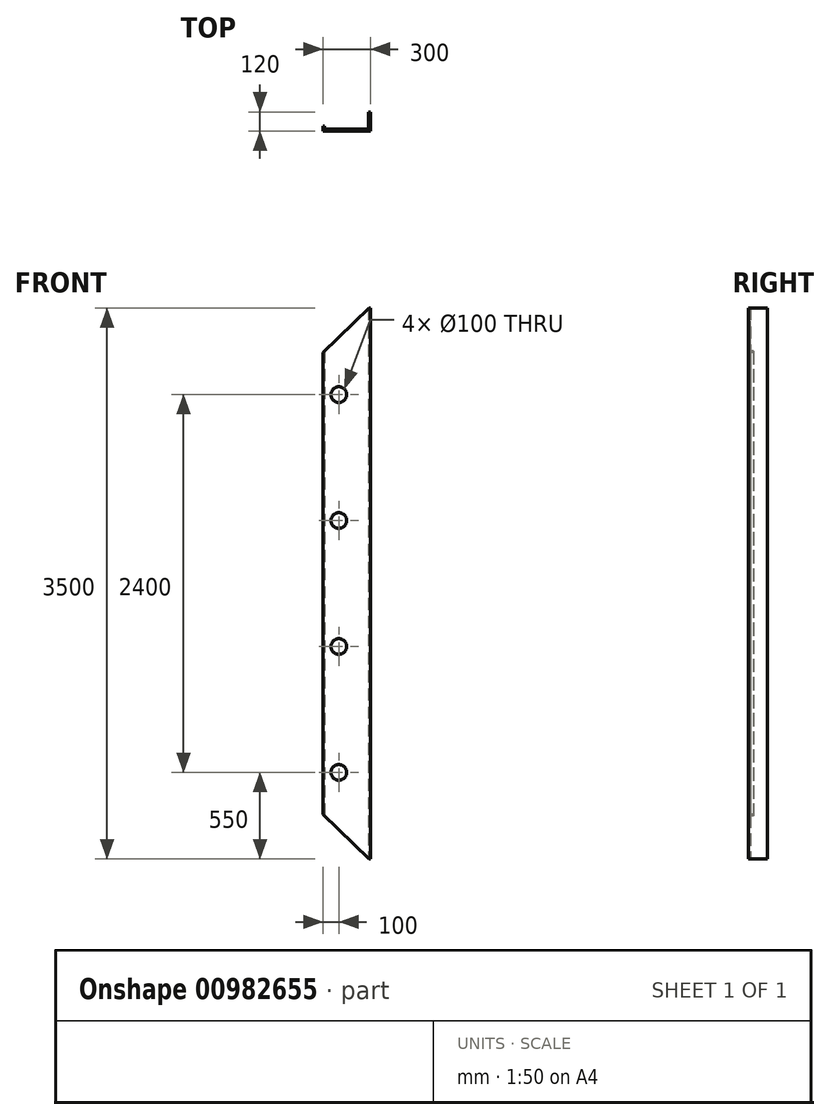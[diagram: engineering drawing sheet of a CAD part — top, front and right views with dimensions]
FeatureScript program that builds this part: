
annotation { "Feature Type Name" : "Feature", "Feature Type Description" : "" }
export const myFeature = defineFeature(function(context is Context, id is Id, definition is map)
    precondition{}
    {
        {
            var Q0;
            Q0=qCreatedBy(makeId("Top.planeOp"),FACE);
            var sketch = newSketch(context, id + "F0", { "sketchPlane" : qUnion([Q0])});
            skLineSegment(sketch, "E0", {"start": v(-110, 0) * mm, "end": v(-100, 0) * mm});
            skLineSegment(sketch, "E1", {"start": v(-100, 0) * mm, "end": v(-100, -20) * mm});
            skLineSegment(sketch, "E2", {"start": v(-100, -20) * mm, "end": v(180, -20) * mm});
            skLineSegment(sketch, "E3", {"start": v(180, -20) * mm, "end": v(180, 90) * mm});
            skLineSegment(sketch, "E4", {"start": v(180, 90) * mm, "end": v(190, 90) * mm});
            skLineSegment(sketch, "E5", {"start": v(190, 90) * mm, "end": v(190, -30) * mm});
            skLineSegment(sketch, "E6", {"start": v(190, -30) * mm, "end": v(-110, -30) * mm});
            skLineSegment(sketch, "E7", {"start": v(-110, -30) * mm, "end": v(-110, 0) * mm});
            skSolve(sketch);
        }
        {
            var Q0;
            Q0=qSketchRegion(id+"F0",true);
            extrude(context, id + "F1", {"entities" : qUnion([Q0]), "depth" : 3500 * mm, "offsetDistance" : 25 * mm});
        }
        {
            var Q0;
            Q0=makeQuery(id+"F1.opExtrude","SWEPT_FACE",FACE,{"disambiguationData":[OSD([sQuery(id+"F0.wireOp",EDGE,"E6")])]});
            var sketch = newSketch(context, id + "F2", { "sketchPlane" : qUnion([Q0])});
            skLineSegment(sketch, "E8", {"start": v(-310, 3024.02) * mm, "end": v(-310, 3700) * mm});
            skLineSegment(sketch, "E9", {"start": v(-310, 3700) * mm, "end": v(390, 3700) * mm});
            skLineSegment(sketch, "E10", {"start": v(390, 3700) * mm, "end": v(-310, 3024.02) * mm});
            skLineSegment(sketch, "E11", {"start": v(-2423.37, 1750) * mm, "end": v(3096.96, 1750) * mm});
            skLineSegment(sketch, "E12.MirrorCS", {"start": v(-310, -200) * mm, "end": v(390, -200) * mm});
            skLineSegment(sketch, "E13.MirrorCS", {"start": v(-310, 475.98) * mm, "end": v(-310, -200) * mm});
            skLineSegment(sketch, "E14.MirrorCS", {"start": v(390, -200) * mm, "end": v(-310, 475.98) * mm});
            skSolve(sketch);
        }
        {
            var Q0;
            {var subQ0=sQuery(id+"F2.wireOp",EDGE,"E14.MirrorCS");var subQ1=sQuery(id+"F0.wireOp",EDGE,"E6");var subQ2=makeQuery(id+"F1.opExtrude","CAP_EDGE",EDGE,{"disambiguationData":[OSD([subQ1])],"isStart":true});var subQ3=makeQuery(id+"F2.imprint","INTERSECT",VERTEX,{"derivedFrom":[subQ2,subQ0]});Q0=makeQuery(id+"F2.imprint","IMPRINT",FACE,{"disambiguationData":[TD([[makeQuery(id+"F2.imprint","IMPRINT",EDGE,{"disambiguationData":[TD([[subQ3,-1.0]])],"derivedFrom":subQ0}),1.0]])]});}
            var Q1;
            {var subQ0=sQuery(id+"F2.wireOp",EDGE,"E10");var subQ1=sQuery(id+"F0.wireOp",EDGE,"E6");var subQ2=makeQuery(id+"F1.opExtrude","CAP_EDGE",EDGE,{"disambiguationData":[OSD([subQ1])],"isStart":false});var subQ3=makeQuery(id+"F2.imprint","INTERSECT",VERTEX,{"derivedFrom":[subQ2,subQ0]});Q1=makeQuery(id+"F2.imprint","IMPRINT",FACE,{"disambiguationData":[TD([[makeQuery(id+"F2.imprint","IMPRINT",EDGE,{"disambiguationData":[TD([[subQ3,-1.0]])],"derivedFrom":subQ0}),-1.0]])]});}
            extrude(context, id + "F3", {"entities" : qUnion([Q0, Q1]), "operationType" : NewBodyOperationType.REMOVE, "oppositeDirection" : true, "depth" : 200 * mm, "offsetDistance" : 25 * mm});
        }
        {
            var Q0;
            Q0=makeQuery(id+"F1.opExtrude","SWEPT_FACE",FACE,{"disambiguationData":[OSD([sQuery(id+"F0.wireOp",EDGE,"E6")])]});
            var sketch = newSketch(context, id + "F4", { "sketchPlane" : qUnion([Q0])});
            skCircle(sketch, "E15", {"center": v(-10, 2950) * mm, "radius": 50 * mm});
            skCircle(sketch, "E16.0.1.0", {"center": v(-10, 2150) * mm, "radius": 50 * mm});
            skCircle(sketch, "E16.0.2.0", {"center": v(-10, 1350) * mm, "radius": 50 * mm});
            skCircle(sketch, "E16.0.3.0", {"center": v(-10, 550) * mm, "radius": 50 * mm});
            skLineSegment(sketch, "E16.direction1", {"start": v(15, 1580) * mm, "end": v(894.74, 1580) * mm, "construction": true});
            skLineSegment(sketch, "E16.direction2", {"start": v(894.74, 1580) * mm, "end": v(894.74, 780) * mm, "construction": true});
            skSolve(sketch);
        }
        {
            var Q0;
            Q0=makeQuery(id+"F4.imprint","IMPRINT",FACE,{"disambiguationData":[TD([[makeQuery(id+"F4.imprint","IMPRINT",EDGE,{"derivedFrom":sQuery(id+"F4.wireOp",EDGE,"E15")}),1.0]])]});
            var Q1;
            Q1=makeQuery(id+"F4.imprint","IMPRINT",FACE,{"disambiguationData":[TD([[makeQuery(id+"F4.imprint","IMPRINT",EDGE,{"derivedFrom":sQuery(id+"F4.wireOp",EDGE,"E16.0.1.0")}),1.0]])]});
            var Q2;
            Q2=makeQuery(id+"F4.imprint","IMPRINT",FACE,{"disambiguationData":[TD([[makeQuery(id+"F4.imprint","IMPRINT",EDGE,{"derivedFrom":sQuery(id+"F4.wireOp",EDGE,"E16.0.2.0")}),1.0]])]});
            var Q3;
            Q3=makeQuery(id+"F4.imprint","IMPRINT",FACE,{"disambiguationData":[TD([[makeQuery(id+"F4.imprint","IMPRINT",EDGE,{"derivedFrom":sQuery(id+"F4.wireOp",EDGE,"E16.0.3.0")}),1.0]])]});
            var Q4;
            Q4=makeQuery(id+"F4.imprint","IMPRINT",FACE,{"disambiguationData":[TD([[makeQuery(id+"F4.imprint","IMPRINT",EDGE,{"derivedFrom":sQuery(id+"F4.wireOp",EDGE,"E16.0.4.0")}),1.0]])]});
            var Q5;
            Q5=makeQuery(id+"F4.imprint","IMPRINT",FACE,{"disambiguationData":[TD([[makeQuery(id+"F4.imprint","IMPRINT",EDGE,{"derivedFrom":sQuery(id+"F4.wireOp",EDGE,"E16.0.5.0")}),1.0]])]});
            var Q6;
            Q6=makeQuery(id+"F4.imprint","IMPRINT",FACE,{"disambiguationData":[TD([[makeQuery(id+"F4.imprint","IMPRINT",EDGE,{"derivedFrom":sQuery(id+"F4.wireOp",EDGE,"E16.0.6.0")}),1.0]])]});
            extrude(context, id + "F5", {"entities" : qUnion([Q0, Q1, Q2, Q3, Q4, Q5, Q6]), "operationType" : NewBodyOperationType.REMOVE, "endBound" : BoundingType.THROUGH_ALL, "oppositeDirection" : true, "depth" : 25 * mm, "offsetDistance" : 25 * mm});
        }
    });
